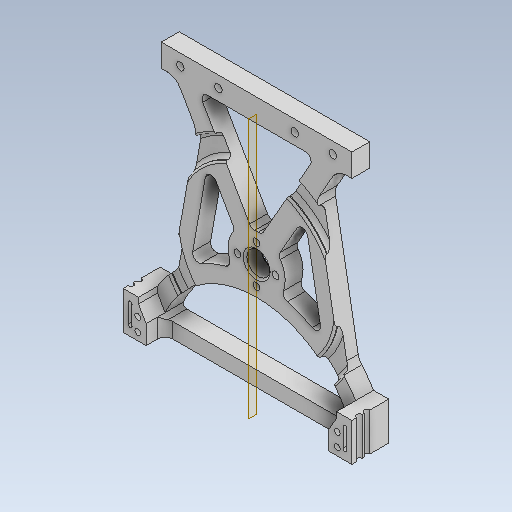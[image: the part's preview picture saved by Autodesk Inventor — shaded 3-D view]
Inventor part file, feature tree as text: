
AUTODESK INVENTOR PART (.ipt)
format: ipt  version: 2020 (Build 240168000, 168)  size: 695,296 bytes
history: native  units: mm
features: sketch x13, extrude x13, projected_geometry x12, fillet x6, mirror x4, thicken_offset x4, reference x4, other x3, plane x2, pattern_circular x1, chamfer x1
ambient origin geometry x8: Origin, YZ Plane, XZ Plane, XY Plane, X Axis, Y Axis, Z Axis, Center Point
bodies: Solid1 (feature_tree)
feature tree (63):
  sketch  "Sketch1"  dims[d0=30.0mm d1=20.0mm]
  plane  "Work Plane1"
  extrude  "Extrusion1"  Depth=20.0mm
  extrude  "Extrusion2"  Depth=4.0mm
  extrude  "Extrusion3"  Depth=10.0mm TaperAngle=0.0deg
  plane  "Work Plane2"
  mirror  "Mirror1"
  extrude  "Extrusion4"  Depth=5.0mm
  extrude  "Extrusion5"  Depth=10.0mm TaperAngle=0.0deg
  extrude  "Extrusion6"  Depth=2.0mm
  fillet  "Fillet1"  Radius=3.5mm
  extrude  "Extrusion7"  Depth=1.5mm
  extrude  "Extrusion8"  Depth=10.0mm
  mirror  "Mirror2"
  fillet  "Fillet2"  Radius=15.0mm
  fillet  "Fillet3"  Radius=3.0mm
  extrude  "Extrusion9"  Depth=4.0mm TaperAngle=0.0deg
  fillet  "Fillet4"  Radius=4.0mm
  thicken_offset  "Thicken1"
  extrude  "Extrusion10"  Depth=1.0mm
  pattern_circular  "Circular Pattern1"  Count=5  [1 undecoded]
  mirror  "Mirror3"
  thicken_offset  "Thicken2"
  thicken_offset  "Thicken3"
  extrude  "Extrusion12"  Depth=5.0mm
  extrude  "Extrusion13"  Depth=1.0mm
  fillet  "Fillet5"  Radius=5.0mm
  fillet  "Fillet6"  Radius=3.0mm
  thicken_offset  "Thicken4"
  chamfer  "Chamfer4"  Distance=4.0mm
  extrude  "Extrusion14"  Depth=1.0mm TaperAngle=0.0deg
  mirror  "Mirror5"
  reference  "Reference1"
  sketch  "Sketch2"  dims[d2=8.0mm d3=4.0mm]
  projected_geometry  "Projected Loop1"
  sketch  "Sketch3"  dims[d4=10.0mm d5=10.0mm d6=0.0mm]
  projected_geometry  "Projected Loop2"
  sketch  "Sketch4"  dims[d7=2.0mm d8=5.0mm]
  projected_geometry  "Projected Loop3"
  projected_geometry  "Projected Loop4"
  sketch  "Sketch5"  dims[d9=30.0deg d10=10.0mm d11=0.0mm]
  projected_geometry  "Projected Loop5"
  sketch  "Sketch6"  dims[d12=2.2mm d13=2.0mm d14=3.5mm]
  projected_geometry  "Projected Loop6"
  sketch  "Sketch7"  dims[d15=1.5mm d16=1.5mm]
  projected_geometry  "Projected Loop7"
  sketch  "Sketch8"  dims[d17=10.0mm d18=0.0mm d19=6.1mm d20=15.0mm d21=3.0mm d22=0.0mm]
  projected_geometry  "Projected Loop8"
  sketch  "Sketch9"  dims[d23=2.5mm d24=4.0mm d25=0.0mm d26=4.0mm]
  reference  "Reference2"
  reference  "Reference3"
  projected_geometry  "Projected Loop9"
  sketch  "Sketch10"  dims[d27=3.0mm d28=0.0mm d29=1.0mm]
  sketch  "Sketch12"  dims[d30=35.0mm]
  projected_geometry  "Projected Loop11"
  sketch  "Sketch13"  dims[d31=6.0mm d32=50.0mm]
  projected_geometry  "Projected Loop12"
  reference  "Reference4"
  sketch  "Sketch14"  dims[d33=20.0mm d34=5.0mm d35=20.0mm d36=5.0mm d37=3.0mm d38=0.0mm d39=4.0mm d40=3.0mm d41=0.0mm d42=1.5mm d43=4.0mm d44=1.5mm d45=1.5mm d46=3.0mm d47=0.0mm d51=2.0mm d52=4.0mm d53=4.0mm d54=5.0mm d55=1.8mm d56=3.0mm d57=0.0mm d58=40.0mm d59=360.0deg d70=1.0mm d71=2.0mm d72=1.0mm d73=2.0mm d74=5.0mm d75=2.0mm d76=5.0mm d77=2.0mm d78=10.0mm d79=2.0mm d80=10.0mm d81=2.0mm d82=9.0mm d83=0.0mm d84=42.0mm d85=53.0mm d86=1.7mm d87=0.0mm d88=1.0mm d89=0.5mm d90=1.7mm d91=1.7mm d95=0.5mm d96=2.0mm d97=45.0deg d98=0.5mm d99=2.0mm d100=2.5mm d101=1.0mm d102=20.0mm d103=0.0mm]
  projected_geometry  "Projected Loop13"
  parser-record x1  (decoder bookkeeping rows leaked as tree rows — omitted from the tree; the rows remain in map.json)
  other  "driver_unit_1.iam"
  other  "driver_wheel_1:1"
note: 1 required parameter value undecoded (feature->parameter linkage not recoverable at this tier; creation-order binding heuristic only, values carry confidence <= 0.55)
note: 1 file-system path scrubbed to <path> (originals preserved in map.json)
